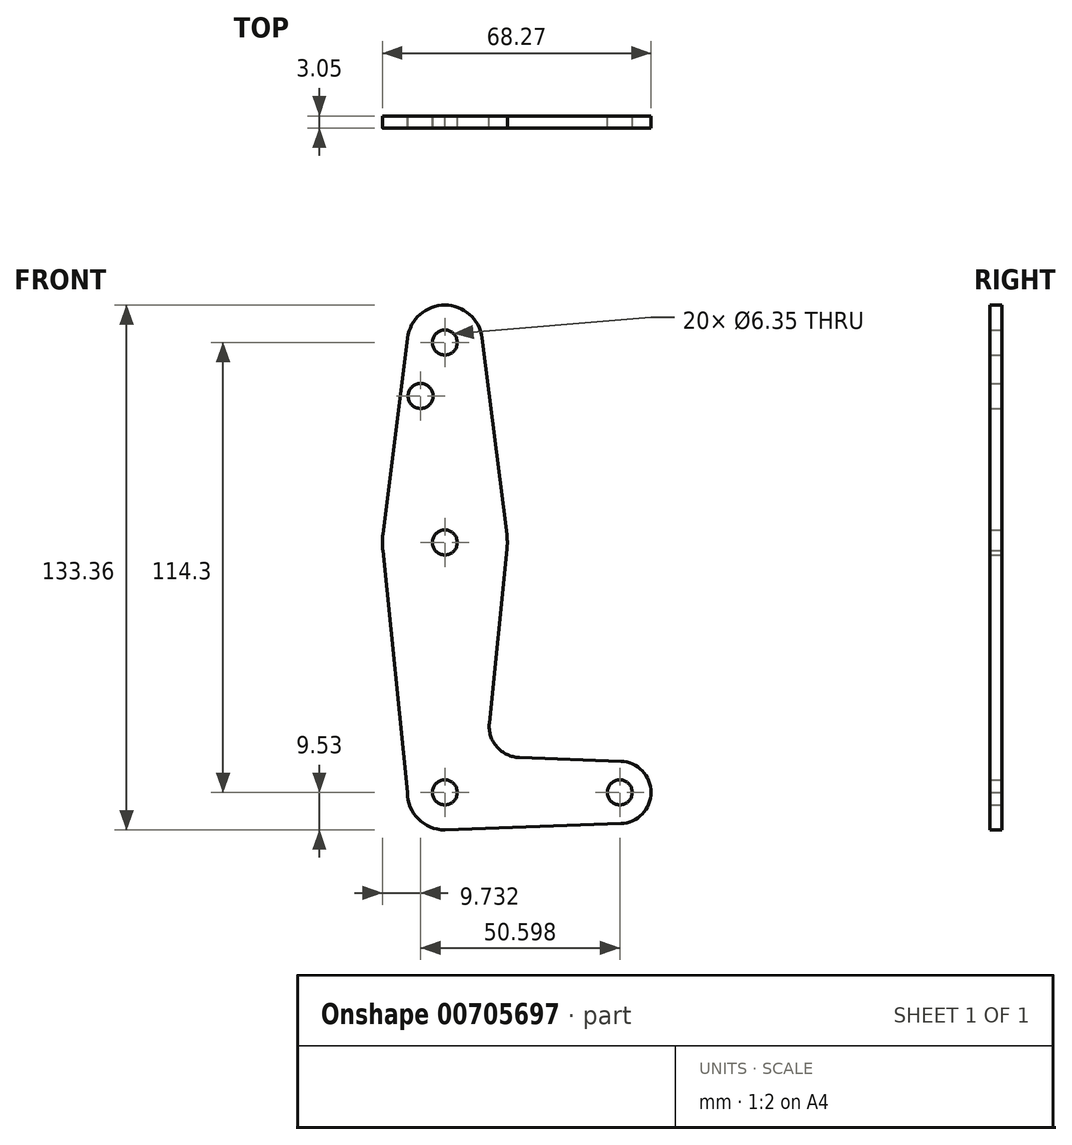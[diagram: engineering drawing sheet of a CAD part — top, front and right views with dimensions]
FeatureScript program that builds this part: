
annotation { "Feature Type Name" : "Feature", "Feature Type Description" : "" }
export const myFeature = defineFeature(function(context is Context, id is Id, definition is map)
    precondition{}
    {
        {
            var Q0;
            Q0=qCreatedBy(makeId("Front.planeOp"),FACE);
            var sketch = newSketch(context, id + "F0", { "sketchPlane" : qUnion([Q0])});
            skLineSegment(sketch, "E0", {"start": v(0, 0) * mm, "end": v(0, 114.3) * mm, "construction": true});
            skLineSegment(sketch, "E1", {"start": v(0, 0) * mm, "end": v(44.45, 0) * mm, "construction": true});
            skCircle(sketch, "E2", {"center": v(44.45, 0) * mm, "radius": 7.94 * mm});
            skCircle(sketch, "E3", {"center": v(0, 0) * mm, "radius": 9.53 * mm});
            skCircle(sketch, "E4", {"center": v(0, 114.3) * mm, "radius": 9.53 * mm});
            skCircle(sketch, "E5", {"center": v(0, 63.5) * mm, "radius": 15.88 * mm});
            skLineSegment(sketch, "E6", {"start": v(-9.45, 115.5) * mm, "end": v(-15.75, 65.48) * mm});
            skLineSegment(sketch, "E7", {"start": v(9.45, 115.5) * mm, "end": v(15.75, 65.48) * mm});
            skLineSegment(sketch, "E8", {"start": v(18.93, 8.85) * mm, "end": v(44.73, 7.93) * mm});
            skLineSegment(sketch, "E9", {"start": v(0, -9.53) * mm, "end": v(44.73, -7.93) * mm});
            skLineSegment(sketch, "E10", {"start": v(-15.75, 61.52) * mm, "end": v(-9.53, 0) * mm});
            skLineSegment(sketch, "E11", {"start": v(15.8, 61.9) * mm, "end": v(11.3, 17.6) * mm});
            skCircle(sketch, "E12", {"center": v(0, 114.3) * mm, "radius": 3.18 * mm});
            skCircle(sketch, "E13", {"center": v(0, 63.5) * mm, "radius": 3.18 * mm});
            skCircle(sketch, "E14", {"center": v(0, 0) * mm, "radius": 3.18 * mm});
            skCircle(sketch, "E15", {"center": v(44.45, 0) * mm, "radius": 3.18 * mm});
            skArc(sketch, "E16.filletArc", {"start": v(11.3, 17.6) * mm, "mid": v(13.22, 11.57) * mm, "end": v(18.93, 8.85) * mm});
            skCircle(sketch, "E17", {"center": v(-6.15, 100.71) * mm, "radius": 3.18 * mm});
            skSolve(sketch);
        }
        {
            var Q0;
            {var subQ0=sQuery(id+"F0.wireOp",EDGE,"E9");var subQ1=sQuery(id+"F0.wireOp",EDGE,"E3");var subQ2=makeQuery(id+"F0.imprint","INTERSECT",VERTEX,{"disambiguationData":[OD(0.0)],"derivedFrom":[subQ1,subQ0]});Q0=makeQuery(id+"F0.imprint","IMPRINT",FACE,{"disambiguationData":[TD([[makeQuery(id+"F0.imprint","IMPRINT",EDGE,{"disambiguationData":[TD([[subQ2,-1.0]])],"derivedFrom":subQ1}),1.0]])]});}
            var Q1;
            Q1=makeQuery(id+"F0.imprint","IMPRINT",FACE,{"disambiguationData":[TD([[makeQuery(id+"F0.imprint","IMPRINT",EDGE,{"derivedFrom":sQuery(id+"F0.wireOp",EDGE,"E15")}),-1.0]])]});
            var Q2;
            {var subQ0=sQuery(id+"F0.wireOp",EDGE,"E8");Q2=makeQuery(id+"F0.imprint","IMPRINT",FACE,{"disambiguationData":[TD([[makeQuery(id+"F0.imprint","IMPRINT",EDGE,{"derivedFrom":subQ0}),-1.0]])]});}
            var Q3;
            Q3=makeQuery(id+"F0.imprint","IMPRINT",FACE,{"disambiguationData":[TD([[makeQuery(id+"F0.imprint","IMPRINT",EDGE,{"derivedFrom":sQuery(id+"F0.wireOp",EDGE,"E14")}),-1.0]])]});
            var Q4;
            Q4=makeQuery(id+"F0.imprint","IMPRINT",FACE,{"disambiguationData":[TD([[makeQuery(id+"F0.imprint","IMPRINT",EDGE,{"derivedFrom":sQuery(id+"F0.wireOp",EDGE,"E13")}),-1.0]])]});
            var Q5;
            {var subQ1=sQuery(id+"F0.wireOp",EDGE,"E6");Q5=makeQuery(id+"F0.imprint","IMPRINT",FACE,{"disambiguationData":[TD([[makeQuery(id+"F0.imprint","IMPRINT",EDGE,{"derivedFrom":subQ1}),1.0]])]});}
            var Q6;
            Q6=makeQuery(id+"F0.imprint","IMPRINT",FACE,{"disambiguationData":[TD([[makeQuery(id+"F0.imprint","IMPRINT",EDGE,{"derivedFrom":sQuery(id+"F0.wireOp",EDGE,"E12")}),-1.0]])]});
            extrude(context, id + "F1", {"entities" : qUnion([Q0, Q1, Q2, Q3, Q4, Q5, Q6]), "depth" : 3.05 * mm, "offsetDistance" : 25.4 * mm});
        }
    });
